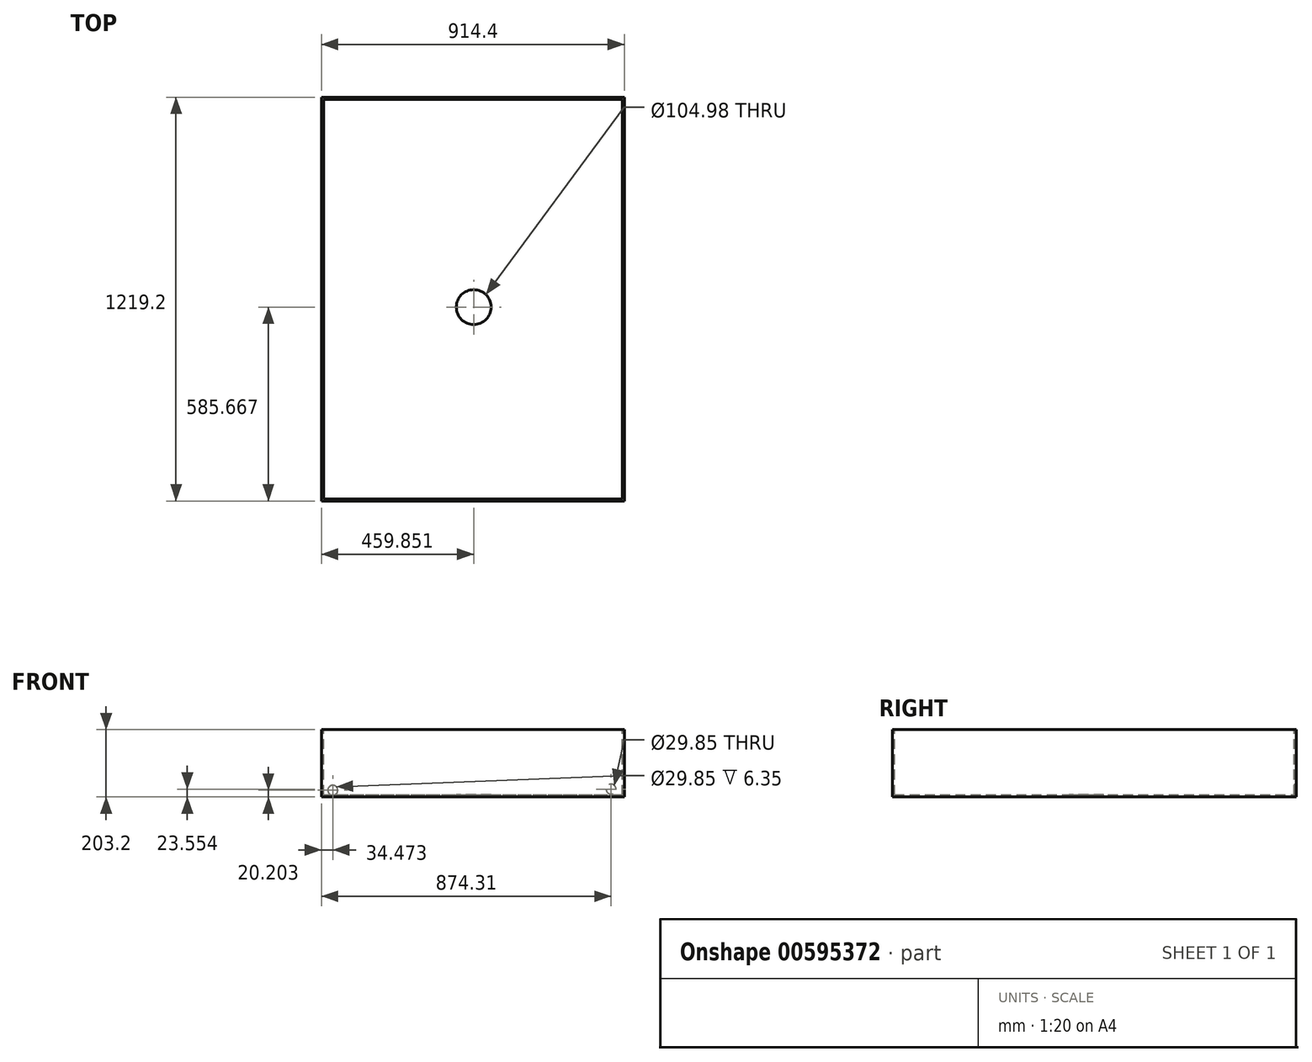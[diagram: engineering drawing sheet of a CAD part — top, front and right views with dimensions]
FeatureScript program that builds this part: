
annotation { "Feature Type Name" : "Feature", "Feature Type Description" : "" }
export const myFeature = defineFeature(function(context is Context, id is Id, definition is map)
    precondition{}
    {
        {
            var Q0;
            Q0=qCreatedBy(makeId("Front.planeOp"),FACE);
            var sketch = newSketch(context, id + "F0", { "sketchPlane" : qUnion([Q0])});
            skLineSegment(sketch, "E0.bottom", {"start": v(0, 0) * mm, "end": v(914.4, 0) * mm});
            skLineSegment(sketch, "E0.top", {"start": v(0, 203.2) * mm, "end": v(914.4, 203.2) * mm});
            skLineSegment(sketch, "E0.left", {"start": v(0, 0) * mm, "end": v(0, 203.2) * mm});
            skLineSegment(sketch, "E0.right", {"start": v(914.4, 0) * mm, "end": v(914.4, 203.2) * mm});
            skSolve(sketch);
        }
        {
            var Q0;
            Q0=makeQuery(id+"F0.imprint","IMPRINT",FACE,{"disambiguationData":[TD([[makeQuery(id+"F0.imprint","IMPRINT",EDGE,{"derivedFrom":sQuery(id+"F0.wireOp",EDGE,"E0.bottom")}),1.0]])]});
            extrude(context, id + "F1", {"entities" : qUnion([Q0]), "depth" : 1219.2 * mm, "offsetDistance" : 25.4 * mm});
        }
        {
            var Q0;
            Q0=makeQuery(id+"F1.opExtrude","SWEPT_FACE",FACE,{"disambiguationData":[OSD([sQuery(id+"F0.wireOp",EDGE,"E0.top")])]});
            shell(context, id + "F2", {"entities" : qUnion([Q0]), "thickness" : 6.35 * mm});
        }
        {
            var Q0;
            Q0=makeQuery(id+"F1.opExtrude","CAP_FACE",FACE,{"disambiguationData":[OSD([sQuery(id+"F0.wireOp",EDGE,"E0.bottom"),sQuery(id+"F0.wireOp",EDGE,"E0.top"),sQuery(id+"F0.wireOp",EDGE,"E0.left"),sQuery(id+"F0.wireOp",EDGE,"E0.right")])],"isStart":true});
            var sketch = newSketch(context, id + "F3", { "sketchPlane" : qUnion([Q0])});
            skCircle(sketch, "E1", {"center": v(-874.31, 23.55) * mm, "radius": 14.92 * mm});
            skCircle(sketch, "E2", {"center": v(-34.47, 20.2) * mm, "radius": 14.92 * mm});
            skSolve(sketch);
        }
        {
            var Q0;
            Q0=makeQuery(id+"F3.imprint","IMPRINT",FACE,{"disambiguationData":[TD([[makeQuery(id+"F3.imprint","IMPRINT",EDGE,{"derivedFrom":sQuery(id+"F3.wireOp",EDGE,"E1")}),1.0]])]});
            var Q1;
            Q1=makeQuery(id+"F3.imprint","IMPRINT",FACE,{"disambiguationData":[TD([[makeQuery(id+"F3.imprint","IMPRINT",EDGE,{"derivedFrom":sQuery(id+"F3.wireOp",EDGE,"E2")}),1.0]])]});
            extrude(context, id + "F4", {"entities" : qUnion([Q0, Q1]), "operationType" : NewBodyOperationType.REMOVE, "oppositeDirection" : true, "depth" : 6.35 * mm, "offsetDistance" : 25.4 * mm});
        }
        {
            var Q0;
            Q0=makeQuery(id+"F2.opShell","OFFSET_FACE",FACE,{"disambiguationData":[OSD([sQuery(id+"F0.wireOp",EDGE,"E0.bottom")])]});
            var sketch = newSketch(context, id + "F5", { "sketchPlane" : qUnion([Q0])});
            skCircle(sketch, "E3", {"center": v(459.85, -633.53) * mm, "radius": 52.5 * mm});
            skSolve(sketch);
        }
        {
            var Q0;
            Q0 = qSketchRegion(id + "F5", true);
            extrude(context, id + "F6", {"entities" : qUnion([Q0]), "operationType" : NewBodyOperationType.REMOVE, "endBound" : BoundingType.THROUGH_ALL, "oppositeDirection" : true, "depth" : 25.4 * mm, "offsetDistance" : 25.4 * mm});
        }
    });
